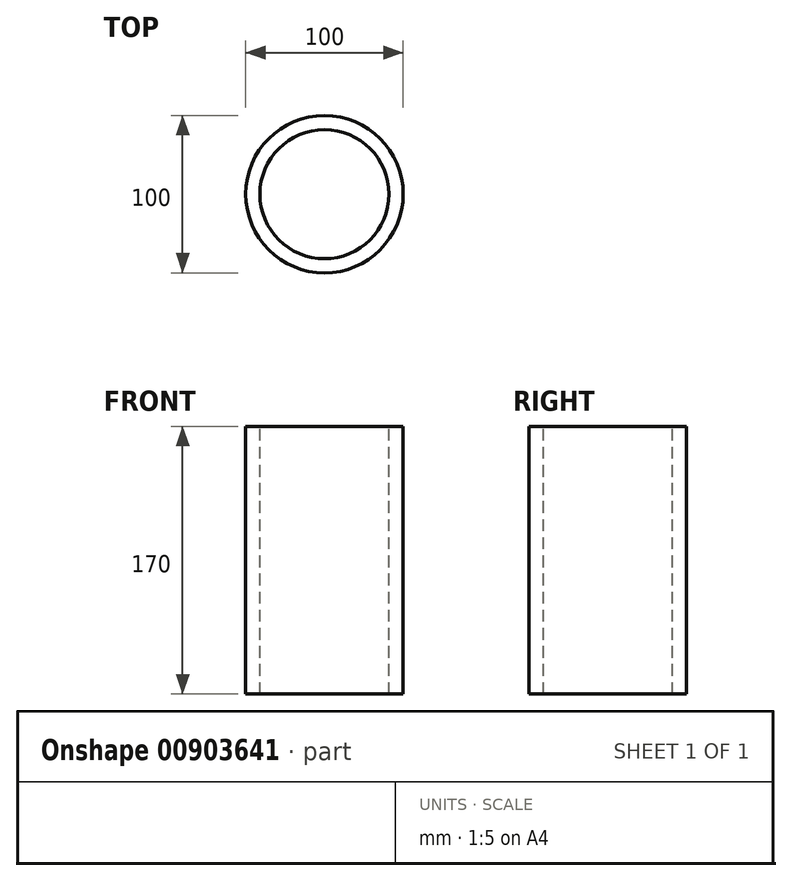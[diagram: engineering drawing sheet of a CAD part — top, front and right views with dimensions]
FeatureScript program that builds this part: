
annotation { "Feature Type Name" : "Feature", "Feature Type Description" : "" }
export const myFeature = defineFeature(function(context is Context, id is Id, definition is map)
    precondition{}
    {
        {
            var Q0;
            Q0=qCreatedBy(makeId("Top.planeOp"),FACE);
            var sketch = newSketch(context, id + "F0", { "sketchPlane" : qUnion([Q0])});
            skCircle(sketch, "E0", {"center": v(0, 0) * mm, "radius": 50 * mm});
            skCircle(sketch, "E1", {"center": v(0, 0) * mm, "radius": 37.5 * mm});
            skCircle(sketch, "E2", {"center": v(0, 0) * mm, "radius": 41 * mm});
            skSolve(sketch);
        }
        {
            var Q0;
            Q0=sQuery(id+"F0.wireOp",EDGE,"E0");
            var Q1;
            Q1=sQuery(id+"F0.wireOp",EDGE,"E2");
            extrude(context, id + "F1", {"bodyType" : ToolBodyType.SURFACE, "surfaceEntities" : qUnion([Q0, Q1]), "depth" : 170 * mm, "offsetDistance" : 25 * mm});
        }
    });
